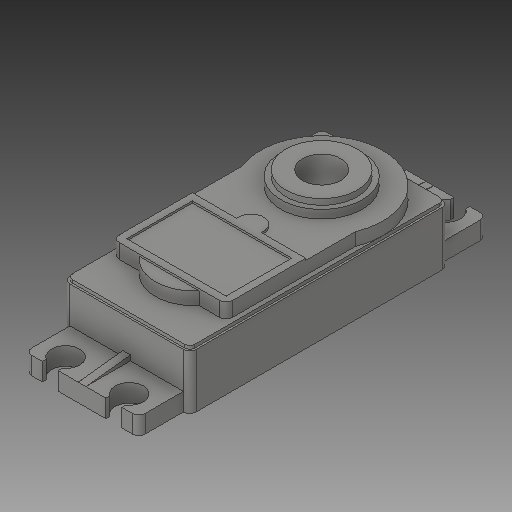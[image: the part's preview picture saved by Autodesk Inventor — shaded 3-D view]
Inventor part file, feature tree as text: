
AUTODESK INVENTOR PART (.ipt)
format: ipt  version: 2017 (Build 210142000, 142)  size: 198,656 bytes
history: native  units: in
note: dims shown in document units (in); Inventor stores cm internally (conversion verified against a paired STEP export)
features: fillet x1
ambient origin geometry x8: Origin, YZ Plane, XZ Plane, XY Plane, X Axis, Y Axis, Z Axis, Center Point
bodies: Solid1 (feature_tree)
feature tree (1):
  fillet  "Fillet2"  [1 undecoded]
note: 1 required parameter value undecoded (feature->parameter linkage not recoverable at this tier; creation-order binding heuristic only, values carry confidence <= 0.55)
